# Revit family: Table-Coffee-Teknion-Zones_ZNTFC-Rectangular-R2015
name_source: partatom
category: Furniture
revit_build: Autodesk Revit Architecture 2016 (Build: 20150220_1215(x64)
units: mm (PartAtom-declared; Revit-internal decimal feet)

## family parameters
Always vertical = Yes
Cut with Voids When Loaded = No
OmniClass Number = 23.40.70.14.64.21
OmniClass Title = Systems Furniture
Room Calculation Point = No
Shared = Yes
Work Plane-Based = No

## types (3) — shared parameters
Assembly Code = E2020200
Height = 36"
Manufacturer = Teknion
Manufacturer Fax = 416.661.4586
Part Number = ZNTFC
Product Documentation Link = http://www.teknion.com
Product Line = Zones
Product Page URL = http://www.teknion.com
Series = Zones
Sustainability Data = http://www.teknion.com
URL = http://www.teknion.com
Warranty = http://www.teknion.com

## per-type parameters (varying)
| type | 38x30 WS Visibility | 42x25 WS Visibility | 48x25 WS Visibility | Depth | Description | Leg Offset | Model | Width |
| 48x25 | No | No | Yes | 25" | Rectangular Coffee Table, 48" Width, 25" Depth | 11 3/4" | ZNTFC4825 | 48" |
| 42x25 | No | Yes | No | 25" | Rectangular Coffee Table, 42" Width, 25" Depth | 9 5/8" | ZNTFC4225 | 42" |
| 38x30 | Yes | No | No | 30" | Rectangular Coffee Table, 38" Width, 30" Depth | 10 3/32" | ZNTFC3830 | 38" |

## geometry (parser evidence)
native form markers: Blend x14, Sweep x2
no freeform markers — native parametric forms only
